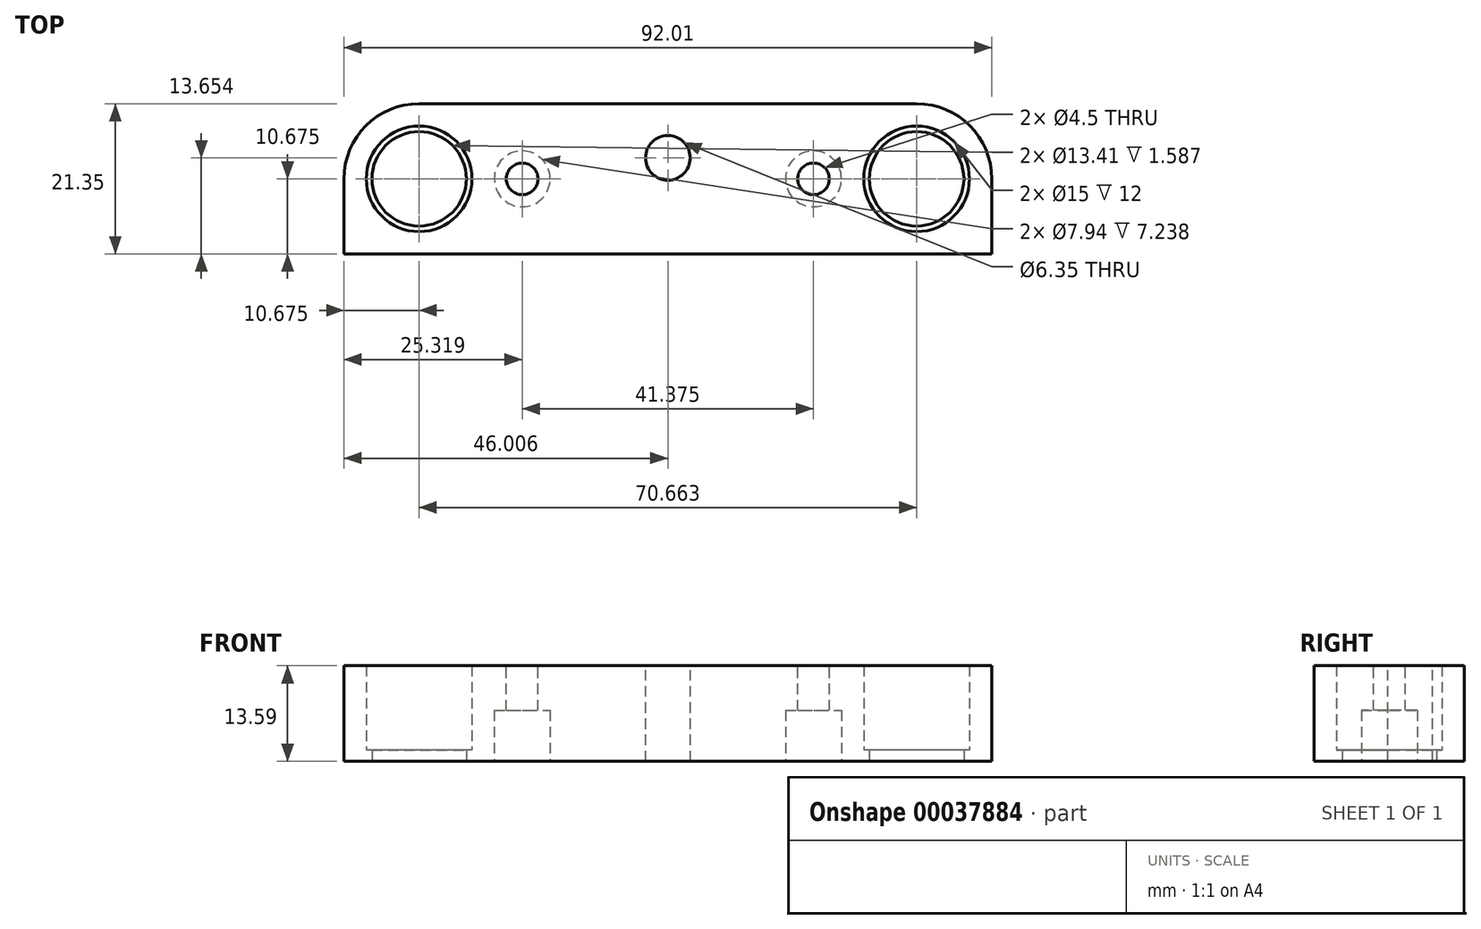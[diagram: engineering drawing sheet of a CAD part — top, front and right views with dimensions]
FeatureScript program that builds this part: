
annotation { "Feature Type Name" : "Feature", "Feature Type Description" : "" }
export const myFeature = defineFeature(function(context is Context, id is Id, definition is map)
    precondition{}
    {
        {
            var Q0;
            Q0=qCreatedBy(makeId("Top.planeOp"),FACE);
            var sketch = newSketch(context, id + "F0", { "sketchPlane" : qUnion([Q0])});
            skLineSegment(sketch, "E0.bottom", {"start": v(0, 0) * mm, "end": v(92.01, 0) * mm});
            skLineSegment(sketch, "E0.top", {"start": v(0, -21.35) * mm, "end": v(92.01, -21.35) * mm});
            skLineSegment(sketch, "E0.left", {"start": v(0, 0) * mm, "end": v(0, -21.35) * mm});
            skLineSegment(sketch, "E0.right", {"start": v(92.01, 0) * mm, "end": v(92.01, -21.35) * mm});
            skLineSegment(sketch, "E1", {"start": v(10.67, 0) * mm, "end": v(10.67, -10.67) * mm, "construction": true});
            skLineSegment(sketch, "E2", {"start": v(10.67, -10.67) * mm, "end": v(0, -10.67) * mm, "construction": true});
            skLineSegment(sketch, "E3", {"start": v(92.01, -10.67) * mm, "end": v(81.34, -10.67) * mm, "construction": true});
            skCircle(sketch, "E4", {"center": v(10.67, -10.67) * mm, "radius": 6.7 * mm});
            skCircle(sketch, "E5", {"center": v(81.34, -10.67) * mm, "radius": 6.7 * mm});
            skSolve(sketch);
        }
        {
            var Q0;
            Q0=qSketchRegion(id+"F0",true);
            extrude(context, id + "F1", {"entities" : qUnion([Q0]), "depth" : 1.59 * mm});
        }
        {
            var Q0;
            Q0=makeQuery(id+"F1.opExtrude","SWEPT_EDGE",EDGE,{"disambiguationData":[OSD([sQuery(id+"F0.wireOp",EDGE,"E0.bottom"),sQuery(id+"F0.wireOp",EDGE,"E0.left")])]});
            var Q1;
            Q1=makeQuery(id+"F1.opExtrude","SWEPT_EDGE",EDGE,{"disambiguationData":[OSD([sQuery(id+"F0.wireOp",EDGE,"E0.bottom"),sQuery(id+"F0.wireOp",EDGE,"E0.right")])]});
            fillet(context, id + "F2", {"entities" : qUnion([Q0, Q1]), "radius" : 10.67 * mm, "tangentPropagation" : true, "allowEdgeOverflow" : false});
        }
        {
            var Q0;
            Q0=makeQuery(id+"F1.opExtrude","CAP_FACE",FACE,{"disambiguationData":[OSD([sQuery(id+"F0.wireOp",EDGE,"E0.bottom"),sQuery(id+"F0.wireOp",EDGE,"E0.top"),sQuery(id+"F0.wireOp",EDGE,"E0.left"),sQuery(id+"F0.wireOp",EDGE,"E0.right"),sQuery(id+"F0.wireOp",EDGE,"E4"),sQuery(id+"F0.wireOp",EDGE,"E5")])],"isStart":false});
            var sketch = newSketch(context, id + "F3", { "sketchPlane" : qUnion([Q0])});
            skLineSegment(sketch, "E6.bottom", {"start": v(0, -10.67) * mm, "end": v(92.01, -10.67) * mm, "construction": true});
            skLineSegment(sketch, "E6.top", {"start": v(0, -15) * mm, "end": v(92.01, -15) * mm});
            skLineSegment(sketch, "E6.left", {"start": v(0, -10.67) * mm, "end": v(0, -15) * mm});
            skLineSegment(sketch, "E6.right", {"start": v(92.01, -10.67) * mm, "end": v(92.01, -15) * mm});
            skLineSegment(sketch, "E7", {"start": v(46, -15) * mm, "end": v(46, -21.35) * mm, "construction": true});
            skPoint(sketch, "E7.endSnap0", {"position": v(46, -21.35) * mm});
            skCircle(sketch, "E8", {"center": v(10.67, -10.67) * mm, "radius": 7.5 * mm});
            skCircle(sketch, "E9", {"center": v(81.34, -10.67) * mm, "radius": 7.5 * mm});
            skSolve(sketch);
        }
        {
            var Q0;
            {var subQ3=makeQuery(id+"F1.opExtrude","CAP_EDGE",EDGE,{"disambiguationData":[OSD([sQuery(id+"F0.wireOp",EDGE,"E0.top")])],"isStart":false});Q0=makeQuery(id+"F3.imprint","IMPRINT",FACE,{"disambiguationData":[TD([[makeQuery(id+"F3.imprint","IMPRINT",EDGE,{"derivedFrom":subQ3}),1.0]])]});}
            var Q1;
            {var subQ9=sQuery(id+"F3.wireOp",EDGE,"E6.left");Q1=makeQuery(id+"F3.imprint","IMPRINT",FACE,{"disambiguationData":[TD([[makeQuery(id+"F3.imprint","IMPRINT",EDGE,{"derivedFrom":subQ9}),1.0]])]});}
            extrude(context, id + "F4", {"entities" : qUnion([Q0, Q1]), "operationType" : NewBodyOperationType.ADD, "depth" : 12 * mm});
        }
        {
            var Q0;
            Q0=makeQuery(id+"F4.opExtrude","CAP_FACE",FACE,{"disambiguationData":[OSD([sQuery(id+"F0.wireOp",EDGE,"E0.bottom"),sQuery(id+"F0.wireOp",EDGE,"E0.top"),sQuery(id+"F0.wireOp",EDGE,"E0.left"),sQuery(id+"F0.wireOp",EDGE,"E0.right"),sQuery(id+"F0.wireOp",EDGE,"E4"),sQuery(id+"F0.wireOp",EDGE,"E5"),sQuery(id+"F3.wireOp",EDGE,"E6.top"),sQuery(id+"F3.wireOp",EDGE,"E6.left"),sQuery(id+"F3.wireOp",EDGE,"E6.right"),sQuery(id+"F3.wireOp",EDGE,"E8"),sQuery(id+"F3.wireOp",EDGE,"E9")])],"isStart":false});
            var sketch = newSketch(context, id + "F5", { "sketchPlane" : qUnion([Q0])});
            skLineSegment(sketch, "E10", {"start": v(25.32, -10.67) * mm, "end": v(66.7, -10.67) * mm, "construction": true});
            skCircle(sketch, "E11", {"center": v(25.32, -10.67) * mm, "radius": 7.14 * mm, "construction": true});
            skPoint(sketch, "E12", {"position": v(46, -10.67) * mm});
            skCircle(sketch, "E13", {"center": v(25.32, -10.67) * mm, "radius": 2.25 * mm});
            skCircle(sketch, "E14", {"center": v(66.7, -10.67) * mm, "radius": 2.25 * mm});
            skLineSegment(sketch, "E15", {"start": v(46, -10.67) * mm, "end": v(46, -21.35) * mm});
            skLineSegment(sketch, "E16", {"start": v(46, -10.67) * mm, "end": v(46, -7.7) * mm});
            skCircle(sketch, "E17", {"center": v(46, -7.7) * mm, "radius": 3.18 * mm});
            skCircle(sketch, "E18.cCircle", {"center": v(46, -7.7) * mm, "radius": 4.52 * mm, "construction": true});
            skLineSegment(sketch, "E18.0", {"start": v(43.4, -3.18) * mm, "end": v(48.62, -3.17) * mm, "construction": true});
            skLineSegment(sketch, "E18.1", {"start": v(48.62, -3.18) * mm, "end": v(51.23, -7.7) * mm, "construction": true});
            skLineSegment(sketch, "E18.2", {"start": v(51.23, -7.7) * mm, "end": v(48.62, -12.22) * mm, "construction": true});
            skLineSegment(sketch, "E18.3", {"start": v(48.62, -12.22) * mm, "end": v(43.4, -12.22) * mm, "construction": true});
            skLineSegment(sketch, "E18.4", {"start": v(43.4, -12.22) * mm, "end": v(40.79, -7.7) * mm, "construction": true});
            skLineSegment(sketch, "E18.5", {"start": v(40.79, -7.7) * mm, "end": v(43.4, -3.18) * mm, "construction": true});
            skPoint(sketch, "E18.0.midPoint", {"position": v(46, -3.18) * mm});
            skLineSegment(sketch, "E19", {"start": v(46, -3.18) * mm, "end": v(46, 0) * mm, "construction": true});
            skSolve(sketch);
        }
        {
            var Q0;
            Q0=qSketchRegion(id+"F5",true);
            var Q1;
            Q1=makeQuery(id+"F1.opExtrude","CAP_FACE",FACE,{"disambiguationData":[OSD([sQuery(id+"F0.wireOp",EDGE,"E0.bottom"),sQuery(id+"F0.wireOp",EDGE,"E0.top"),sQuery(id+"F0.wireOp",EDGE,"E0.left"),sQuery(id+"F0.wireOp",EDGE,"E0.right"),sQuery(id+"F0.wireOp",EDGE,"E4"),sQuery(id+"F0.wireOp",EDGE,"E5")])],"isStart":true});
            extrude(context, id + "F6", {"entities" : qUnion([Q0]), "operationType" : NewBodyOperationType.REMOVE, "endBound" : BoundingType.UP_TO_SURFACE, "oppositeDirection" : true, "endBoundEntityFace" : qUnion([Q1]), "depth" : 25.4 * mm});
        }
        {
            var Q0;
            Q0=makeQuery(id+"F1.opExtrude","CAP_FACE",FACE,{"disambiguationData":[OSD([sQuery(id+"F0.wireOp",EDGE,"E0.bottom"),sQuery(id+"F0.wireOp",EDGE,"E0.top"),sQuery(id+"F0.wireOp",EDGE,"E0.left"),sQuery(id+"F0.wireOp",EDGE,"E0.right"),sQuery(id+"F0.wireOp",EDGE,"E4"),sQuery(id+"F0.wireOp",EDGE,"E5")])],"isStart":true});
            var sketch = newSketch(context, id + "F7", { "sketchPlane" : qUnion([Q0])});
            skCircle(sketch, "E20", {"center": v(66.7, 10.67) * mm, "radius": 3.97 * mm});
            skCircle(sketch, "E21", {"center": v(25.32, 10.67) * mm, "radius": 3.97 * mm});
            skSolve(sketch);
        }
        {
            var Q0;
            Q0=qSketchRegion(id+"F7",true);
            extrude(context, id + "F8", {"entities" : qUnion([Q0]), "operationType" : NewBodyOperationType.REMOVE, "oppositeDirection" : true, "depth" : 7.24 * mm});
        }
    });
